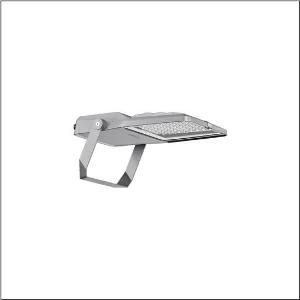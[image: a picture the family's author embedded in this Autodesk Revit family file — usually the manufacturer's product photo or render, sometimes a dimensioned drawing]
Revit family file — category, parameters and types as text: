
# Revit family: floodlight_fl_21_iq_mini___pl52_5xa7771c2d1a_0a7e
name_source: partatom
category: Lighting Fixtures
units: mm (PartAtom-declared; Revit-internal decimal feet)

## family parameters
Cut with Voids When Loaded = No
Host = Face
Light Source = No
Part Type = Normal
Room Calculation Point = No
Round Connector Dimension = Use Diameter
Shared = No

## types (1)
- --- (1 x LED, 12210 lm, 87.2 W, 3000K)
    Apparent Load = 87 VA
    CIE Flux Codes = 26 60 98 100 100
    Color Rendering = 70
    Color Temperature = 3000K
    Default Elevation = 1800 mm
    Description = Floodlight FL 21 iQ mini, floodlight, primary light control with lens, of PMMA, primary optical cover: protective disc, of toughened safety glass, transparent, light distribution: PL52, light emission: direct distribution, installation type: surface-mounted, LED, High Power LED, rated luminous flux: 12.210lm, luminous efficacy: 140lm/W, light colour: 730, colour temperature: 3000K, control: Auto-Match, Temp-Guard, Lumen-Switch, Night-Set, Smart-Wire, Light-Fading, Desk-Remote (wireless, voltage-free reading and setting of iQ features in the workshop via application-optimized NFC function/RFID function), optimised constant luminous flux control (CLO 2.0), with terminal, 6-pole, mains connection: 220..240V, AC, 50/60Hz, start of lifetime: 87W, end of service life: 92W, reduction: 40W, luminaire housing, of diecast aluminium, powder-coated, Siteco® metallic grey (DB 702S), corrosivity category C5 mid according to DIN EN ISO 12944, sealing non-destructively replaceable, mounting bracket, of steel, galvanised, powder-coated, Siteco® metallic grey (DB 702S), protection rating (complete): IP66, insulation class (complete): insulation class II (safety insulation), certification: CE, ENEC, VDE, protection symbol: D, impact resistance: IK08, permissible operating ambient temperature: -40..+40°C, permissible operating ambient temperature for outdoor applications: -40..+50°C, standard: DIN EN 12944, LABS conformity tested according to VDMA 24364:2018-05, packaging unit: 1 piece

Light Distribution: PL52
    Height = 70 mm
    Lamp = 1 x LED
    Lamp Light Flux = 12210 lm
    Lamp Power = 87.2 W
    Lamp count = 1
    Length = 485 mm
    Luminous efficacy = 140 lm/W
    Manufacturer = Siteco
    ModVariant = No
    Model = 5XA7771C2D1A
    Number of Poles = 1
    OnlyDefault = Yes
    Power Factor = 1
    Product Name = Floodlight FL 21 iQ mini | PL52
    Product group = floodlight | pylon annexe
    ProductGroupID = 6200
    Protection Class = Protection class II
    Protection Degree = IP 66
    RLX_Detail_Level = 1
    RLX_Emergency_Light_Flux = 0 lm
    RLX_Emergency_Type = 0
    RLX_Emergency_Type_DB = No
    RlxData = <blob elided: 96509 chars, md5=5323fe7d>
    Socket = socket
    Standby Power = 0 W
    System Light Flux = 12210 lm
    System Power = 87 W
    Type Comments = factory setting: luminous flux: 100 % | dim-lin: 254 | 456 mA
    Type Image = l_1006845.jpg
    URL = http://relux.com
    VarID = @adj_096927
    Voltage = 0 V
    Weight = 0.00 kg
    Width = 337 mm

## geometry (parser evidence)
native form markers: Blend x4, Sweep x11
no freeform markers — native parametric forms only
